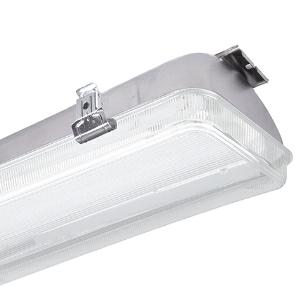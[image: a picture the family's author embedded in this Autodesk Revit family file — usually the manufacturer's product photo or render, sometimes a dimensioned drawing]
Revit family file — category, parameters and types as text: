
# Revit family: 3f_filippi_-_beta_235_92_pc_ampio_3f_filippi_-_52867_-_beta_235_led_922x40_ampio_l1265
name_source: partatom
category: Lighting Fixtures
units: mm (PartAtom-declared; Revit-internal decimal feet)

## family parameters
Cut with Voids When Loaded = No
Host = Face
Light Source = No
Part Type = Normal
Room Calculation Point = No
Round Connector Dimension = Use Diameter
Shared = No

## types (1)
- 3F Filippi - Beta 235 92 PC Ampio (1 x LED, 12843 lm, 80 W, 4000 K)
    Apparent Load = 80 VA
    Approval mark = CE
    CIE Flux Codes = 59 89 98 98 100
    Color Rendering = 80
    Color Temperature = 4000 K
    Control Gear = Electronic ballast
    Default Elevation = 1800 mm
    Description = ILLUMINOTECHNICAL
Luminous efficiency 100% (DLOR 99%, ULOR 1%).
Initial luminous flux of the luminaire 12843 lm.
Wide symmetric distribution.
Installation Interdistance Transv.D = 1.40 x hu - Long.D = 1.43 x hu.
Tabular UGR (CIE 117 - 4H-8H; S=0.25H; 70/50/20): RUG 20.9 - 21.5.
Beam angle: 98° - 100°.
Luminous efficacy 161 lm/W.
Lifetime (L93/B10): 30000 h. (tq+25°C)
Lifetime (L90/B10): 50000 h. (tq+25°C)
Lifetime (L85/B10): 80000 h. (tq+25°C)
Lifetime (L80/B10): 100000 h. (tq+25°C)
Lifetime (L85/B10): 50000 h. (tq+45°C)
Sudden decreased luminous flux after 50000 hours: 0% (C0).
Photobiological safety in compliance with IEC/TR 62778: RG0 risk exempt, (IEC 62471).
In compliance with IEC/EN 62722-2-1 - IEC/EN 62717 standards.

SOURCE
2 linear LED modules 40W/840.
Energy efficiency class (UE 2019/2020 - UE 2019/2015): C.
CIE 13.3 Colour rendering index: CRI >80 (R9 <50%).
IES TM-30 Fidelity Index: Rf = 84 Rg = 95.
CCT nominal colour temperature 4000 K.
Colour initial tolerance (MacAdam): SDCM 3.

MECHANICAL
Housing in AISI 304 stainless steel, pressed in one single piece.
Polycarbonate screen etched internally, V2 self-extinguishing, UV stabilised, injection moulded.
Ecologic anti-aging sealing gasket.
Oversized gear-tray reflector unit in highly reflective white painted hot-galvanised steel.
Methacrylate (PMMA) lenses with external flat surface.
Stainless steel snap-lock clips for diffuser mounting (safety n° 4 per fixture).
Luminaire with limited surface temperature. - D - (EN 60598-2-24)
Dimensions: 1265x235 mm, height 135 mm. Weight 7.045 kg.
IP65 protection degree.
Mechanical strength to impacts IK10 (20 joule).
Glow-wire test resistance 850°C.

ELECTRICAL
Halogen Free electronic wiring 230V-50/60Hz, power factor 0.95, THD <25%, constant output current, class I, 1 driver.
Power of the luminaire 80 W.
ENEC - CE.
Flicker: <4%.
Luminaire compliant with EN 60598-2-22 for power supply from a centralised emergency system CPSS (Central Power Supply System), not incorporated in the luminaire - high risk areas excluded. The default power and flux are 100% in AC and 100% in DC.
Ambient temperature from -20°C to +45°C.
Temperature class T6 max 85°C.
Quick connection via M20 3P connector with 9-13 mm tightening range.
Relative humidity UR: <85%.

INSTALLATION
Ceiling / Suspended / Wall.
All accessories dedicated to this product are available on the Catalog and on our website www.3F-Filippi.com.

APPLICATIONS
Suitable product for food production plants (HACCP), IFS (Food Version 6), BRC (GSFS Food Version 7).
Dry, dusty indoor environments, subject to occasional water splashes.
Any environments except the ones where the luminaire materials are unsuitable.
Industrial environments, warehouses, environments where security locks are required on all clips, e.g. prisons (on request).
Environments in which it is necessary a total protection against falling fragments (eg environments with foodstuffs or machines with moving parts or with extreme temperature changes), use luminaires with laminated glass.
Tempered glass is not immune to falling fragments from harmless and caused by shocks or exceptionally derived from the tempering process.

WARNING
Fixture not suitable for cold stores with an ambient temperature <0°C and/or relative humidity >85%.
Luminaire designed for disposal/recycling at end-of-life.
Replaceable (LED only) light source by a professional. Replaceable control gear by a professional.
    Height = 135 mm
    Lamp = 1 x LED
    Lamp Light Flux = 12843 lm
    Lamp Power = 80 W
    Lamp count = 1
    Length = 1265 mm
    Lifetime = 50000 h
    Luminous efficacy = 161 lm/W
    Manufacturer = 3F Filippi
    ModVariant = No
    Model = 3F Filippi - 52867 - Beta 235 LED 922x40 AMPIO L1265
    Mounting Place = Ceiling
    Mounting Type = Pendant
    Number of Poles = 1
    OnlyDefault = Yes
    Power Factor = 1
    Product Name = 3F Filippi - Beta 235 92 PC Ampio
    Product group = pendant luminaire
    ProductGroupID = 9
    Protection Class = Protection class I
    Protection Degree = IP 65
    RLX_Detail_Level = 1
    RLX_Emergency_Light_Flux = 0 lm
    RLX_Emergency_Type = 0
    RLX_Emergency_Type_DB = No
    RlxData = <blob elided: 91737 chars, md5=7467beac>
    Socket = socket
    Standby Power = 0 W
    System Light Flux = 12843 lm
    System Power = 80 W
    Type Comments = Product without accessories
    Type Image = 3ffilippi_52867.jpg
    URL = http://relux.com
    VarID = ---
    Voltage = 0 V
    Weight = 0.00 kg
    Width = 235 mm

## geometry (parser evidence)
native form markers: Blend x4, Sweep x9
no freeform markers — native parametric forms only
